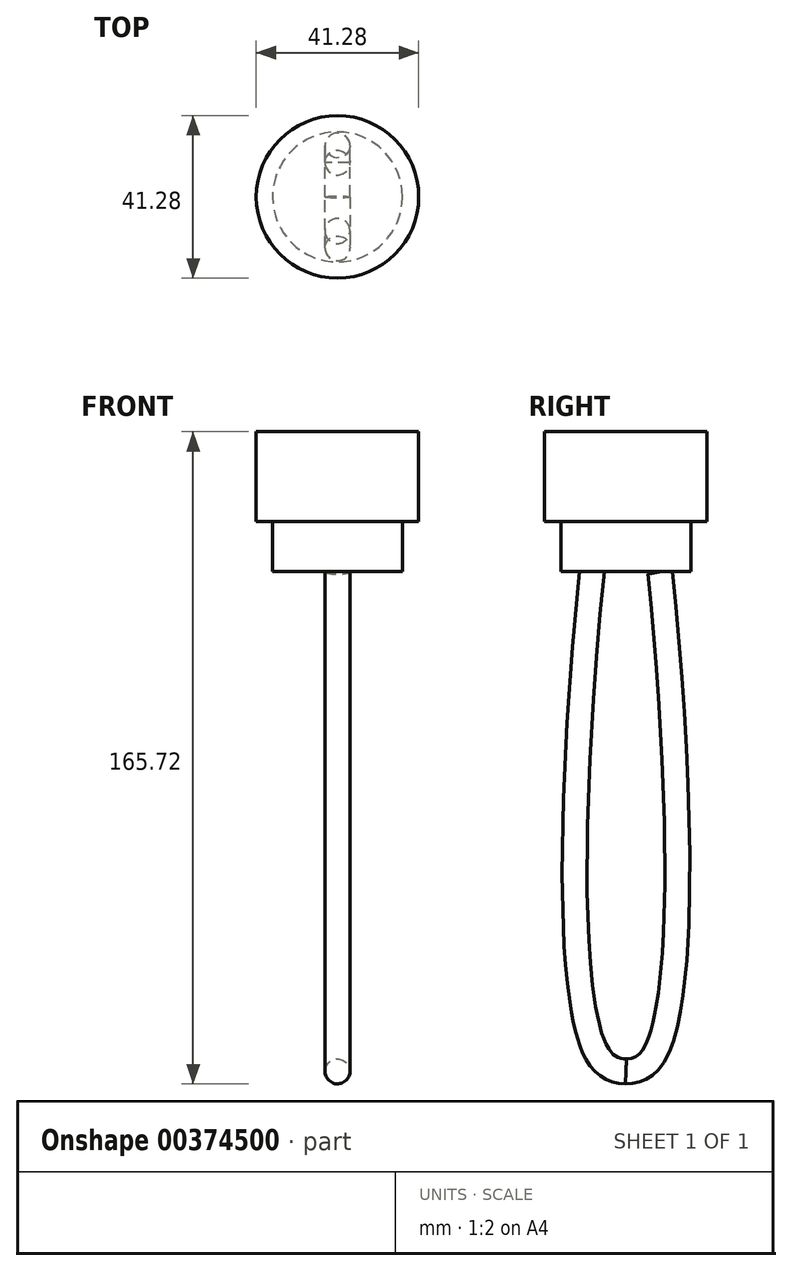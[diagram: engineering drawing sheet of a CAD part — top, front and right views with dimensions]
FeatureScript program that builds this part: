
annotation { "Feature Type Name" : "Feature", "Feature Type Description" : "" }
export const myFeature = defineFeature(function(context is Context, id is Id, definition is map)
    precondition{}
    {
        {
            var Q0;
            Q0=qCreatedBy(makeId("Top.planeOp"),FACE);
            var sketch = newSketch(context, id + "F0", { "sketchPlane" : qUnion([Q0])});
            skCircle(sketch, "E0", {"center": v(0, 0) * mm, "radius": 20.64 * mm});
            skSolve(sketch);
        }
        {
            var Q0;
            Q0 = qSketchRegion(id + "F0", true);
            extrude(context, id + "F1", {"entities" : qUnion([Q0]), "depth" : 22.86 * mm});
        }
        {
            var Q0;
            Q0=makeQuery(id+"F1.opExtrude","CAP_FACE",FACE,{"disambiguationData":[OSD([sQuery(id+"F0.wireOp",EDGE,"E0")])],"isStart":true});
            var sketch = newSketch(context, id + "F2", { "sketchPlane" : qUnion([Q0])});
            skCircle(sketch, "E1", {"center": v(0, 0) * mm, "radius": 16.51 * mm});
            skSolve(sketch);
        }
        {
            var Q0;
            Q0 = qSketchRegion(id + "F2", true);
            extrude(context, id + "F3", {"entities" : qUnion([Q0]), "operationType" : NewBodyOperationType.ADD, "depth" : 12.7 * mm});
        }
        {
            var Q0;
            Q0=makeQuery(id+"F3.opExtrude","CAP_FACE",FACE,{"disambiguationData":[OSD([sQuery(id+"F2.wireOp",EDGE,"E1")])],"isStart":false});
            var sketch = newSketch(context, id + "F4", { "sketchPlane" : qUnion([Q0])});
            skCircle(sketch, "E2", {"center": v(0, 8.66) * mm, "radius": 3.18 * mm});
            skSolve(sketch);
        }
        {
            var Q0;
            Q0=qCreatedBy(makeId("Right.planeOp"),FACE);
            var sketch = newSketch(context, id + "F5", { "sketchPlane" : qUnion([Q0])});
            skPoint(sketch, "E3", {"position": v(-10.16, -127) * mm});
            skPoint(sketch, "E4", {"position": v(0, -139.7) * mm});
            skFitSpline(sketch, "E5", {"points": [v(0, -139.7) * mm, v(-10.16, -127) * mm, v(-8.66, -12.7) * mm], "startDerivative": vector(-62.1, 0.52) * mm, "endDerivative": vector(19.56, 186.92) * mm});
            skFitSpline(sketch, "E6.MirrorCS", {"points": [v(0, -139.7) * mm, v(10.16, -127) * mm, v(8.66, -12.7) * mm], "startDerivative": vector(62.1, 0.52) * mm, "endDerivative": vector(-19.56, 186.92) * mm});
            skSolve(sketch);
        }
        {
            var Q0;
            Q0=makeQuery(id+"F4.imprint","IMPRINT",FACE,{"disambiguationData":[TD([[makeQuery(id+"F4.imprint","IMPRINT",EDGE,{"derivedFrom":sQuery(id+"F4.wireOp",EDGE,"E2")}),1.0]])]});
            var Q1;
            Q1=sQuery(id+"F5.wireOp",EDGE,"E5");
            var Q2;
            Q2=sQuery(id+"F5.wireOp",EDGE,"E6.MirrorCS");
            sweep(context, id + "F6", {"operationType" : NewBodyOperationType.ADD, "profiles" : qUnion([Q0]), "path" : qUnion([Q1, Q2])});
        }
    });
